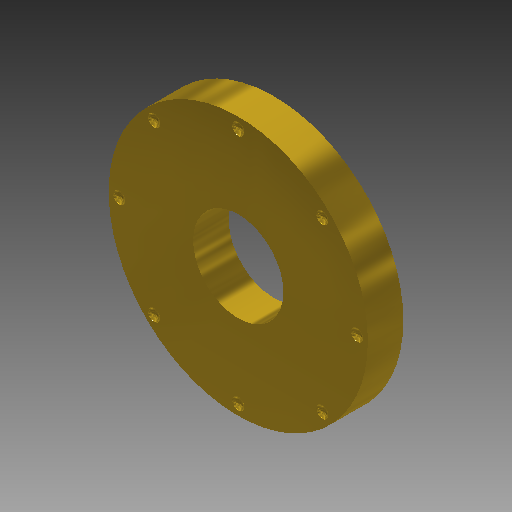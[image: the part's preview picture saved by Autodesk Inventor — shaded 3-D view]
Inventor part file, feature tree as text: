
AUTODESK INVENTOR PART (.ipt)
format: ipt  version: 2017 (Build 210142000, 142)  size: 151,040 bytes
history: native  units: mm (DEFAULTED — no unit token found)
features: sketch x4, revolve x2, pattern_circular x2, extrude x1
ambient origin geometry x8: Origin, YZ Plane, XZ Plane, XY Plane, X Axis, Y Axis, Z Axis, Center Point
bodies: Solid1 (feature_tree)
feature tree (9):
  extrude  "Extrusion1"  Depth=36.5mm
  sketch  "Sketch2"  dims[d2=5.0mm d3=0.0mm d4=14.2mm]
  revolve  "Revolution1"  [1 undecoded]
  pattern_circular  "Circular Pattern1"  [2 undecoded]
  revolve  "Revolution2"  [1 undecoded]
  pattern_circular  "Circular Pattern2"  Angle=90.0deg  [1 undecoded]
  sketch  "Sketch1"  dims[d0=12.7mm d1=36.5mm]
  sketch  "Sketch3"  dims[d5=1.5mm]
  sketch  "Sketch4"  dims[d6=1.5mm d9=0.5mm d10=2.0mm d11=90.0deg d12=80.0mm d13=360.0deg d15=1.5mm d16=0.5mm d17=2.0mm d18=90.0deg d19=60.0mm d20=360.0deg]
note: 5 required parameter values undecoded (feature->parameter linkage not recoverable at this tier; creation-order binding heuristic only, values carry confidence <= 0.55)